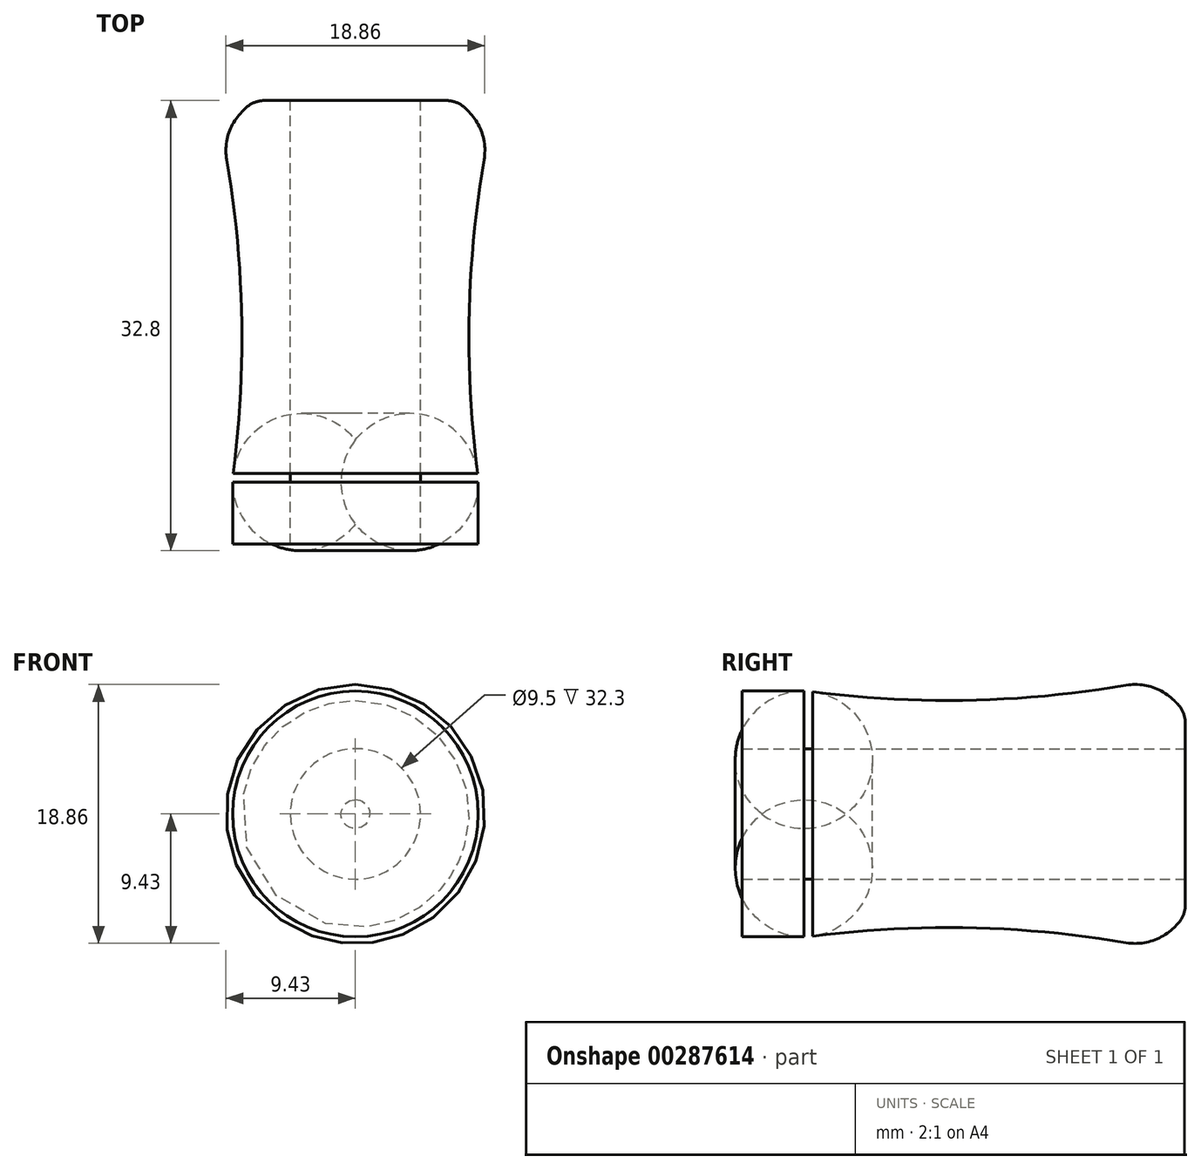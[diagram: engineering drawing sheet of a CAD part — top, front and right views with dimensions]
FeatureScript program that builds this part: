
annotation { "Feature Type Name" : "Feature", "Feature Type Description" : "" }
export const myFeature = defineFeature(function(context is Context, id is Id, definition is map)
    precondition{}
    {
        {
            var Q0;
            Q0=qCreatedBy(makeId("Top.planeOp"),FACE);
            var sketch = newSketch(context, id + "F0", { "sketchPlane" : qUnion([Q0])});
            skLineSegment(sketch, "E0", {"start": v(-4.75, 13.53) * mm, "end": v(-4.75, -21.77) * mm, "construction": true});
            skLineSegment(sketch, "E1.MirrorCS", {"start": v(4.75, 13.53) * mm, "end": v(4.75, -21.77) * mm, "construction": true});
            skLineSegment(sketch, "E2.bottom", {"start": v(9.75, 15) * mm, "end": v(-0.25, 15) * mm, "construction": true});
            skLineSegment(sketch, "E2.top", {"start": v(9.75, -15) * mm, "end": v(-0.25, -15) * mm, "construction": true});
            skLineSegment(sketch, "E2.left", {"start": v(9.75, 15) * mm, "end": v(9.75, -15) * mm, "construction": true});
            skLineSegment(sketch, "E2.right", {"start": v(-0.25, 15) * mm, "end": v(-0.25, -15) * mm, "construction": true});
            skPoint(sketch, "E2.middle", {"position": v(4.75, 0) * mm});
            skArc(sketch, "E3", {"start": v(9.38, 12.98) * mm, "mid": v(8.28, -1.03) * mm, "end": v(9.75, -15) * mm});
            skLineSegment(sketch, "E4", {"start": v(8.26, 16.49) * mm, "end": v(7.45, 17.3) * mm});
            skLineSegment(sketch, "E5", {"start": v(7.45, 17.3) * mm, "end": v(4.75, 17.3) * mm});
            skLineSegment(sketch, "E6", {"start": v(4.75, 17.3) * mm, "end": v(4.75, -15) * mm});
            skLineSegment(sketch, "E7", {"start": v(4.75, -15) * mm, "end": v(9.75, -15) * mm});
            skPoint(sketch, "E8.visualSharp", {"position": v(9.75, 15) * mm});
            skArc(sketch, "E8.filletArc", {"start": v(9.38, 12.98) * mm, "mid": v(9.25, 14.87) * mm, "end": v(8.26, 16.49) * mm});
            skLineSegment(sketch, "E9", {"start": v(0, 32.98) * mm, "end": v(0, -42.15) * mm, "construction": true});
            skSolve(sketch);
        }
        {
            var Q0;
            Q0=makeQuery(id+"F0.imprint","IMPRINT",FACE,{"disambiguationData":[TD([[makeQuery(id+"F0.imprint","IMPRINT",EDGE,{"derivedFrom":sQuery(id+"F0.wireOp",EDGE,"E3")}),-1.0]])]});
            var Q1;
            Q1=sQuery(id+"F0.wireOp",EDGE,"E9");
            revolve(context, id + "F1", {"entities" : qUnion([Q0]), "axis" : qUnion([Q1]), "revolveType" : RevolveType.FULL});
        }
        {
            var Q0;
            Q0=makeQuery(id+"F1.opRevolve","SWEPT_EDGE",EDGE,{"disambiguationData":[OSD([sQuery(id+"F0.wireOp",EDGE,"E4"),sQuery(id+"F0.wireOp",EDGE,"E5")])]});
            fillet(context, id + "F2", {"entities" : qUnion([Q0]), "radius" : 2 * mm, "tangentPropagation" : true, "allowEdgeOverflow" : false});
        }
        {
            var Q0;
            Q0=makeQuery(id+"F1.opRevolve","SWEPT_FACE",FACE,{"disambiguationData":[OSD([sQuery(id+"F0.wireOp",EDGE,"E7")])]});
            var sketch = newSketch(context, id + "F3", { "sketchPlane" : qUnion([Q0])});
            skCircle(sketch, "E10", {"center": v(0, 0) * mm, "radius": 8.95 * mm});
            skSolve(sketch);
        }
        {
            var Q0;
            Q0=makeQuery(id+"F3.imprint","IMPRINT",FACE,{"disambiguationData":[TD([[makeQuery(id+"F3.imprint","IMPRINT",EDGE,{"derivedFrom":sQuery(id+"F3.wireOp",EDGE,"E10")}),-1.0]])]});
            var Q1;
            Q1=makeQuery(id+"F1.opRevolve","SWEPT_FACE",FACE,{"disambiguationData":[OSD([sQuery(id+"F0.wireOp",EDGE,"E8.filletArc")])]});
            extrude(context, id + "F4", {"entities" : qUnion([Q0]), "operationType" : NewBodyOperationType.REMOVE, "oppositeDirection" : true, "endBoundEntityFace" : qUnion([Q1]), "depth" : 10 * mm});
        }
        {
            var Q0;
            Q0=makeQuery(id+"F4.boolean.opBoolean","INTERSECT",EDGE,{"derivedFrom":[makeQuery(id+"F1.opRevolve","SWEPT_FACE",FACE,{"disambiguationData":[OSD([sQuery(id+"F0.wireOp",EDGE,"E3")])]}),makeQuery(id+"F4.opExtrude","SWEPT_FACE",FACE,{"disambiguationData":[OSD([sQuery(id+"F3.wireOp",EDGE,"E10")])]})]});
            fillet(context, id + "F5", {"entities" : qUnion([Q0]), "radius" : 5 * mm, "tangentPropagation" : true, "allowEdgeOverflow" : false});
        }
    });
